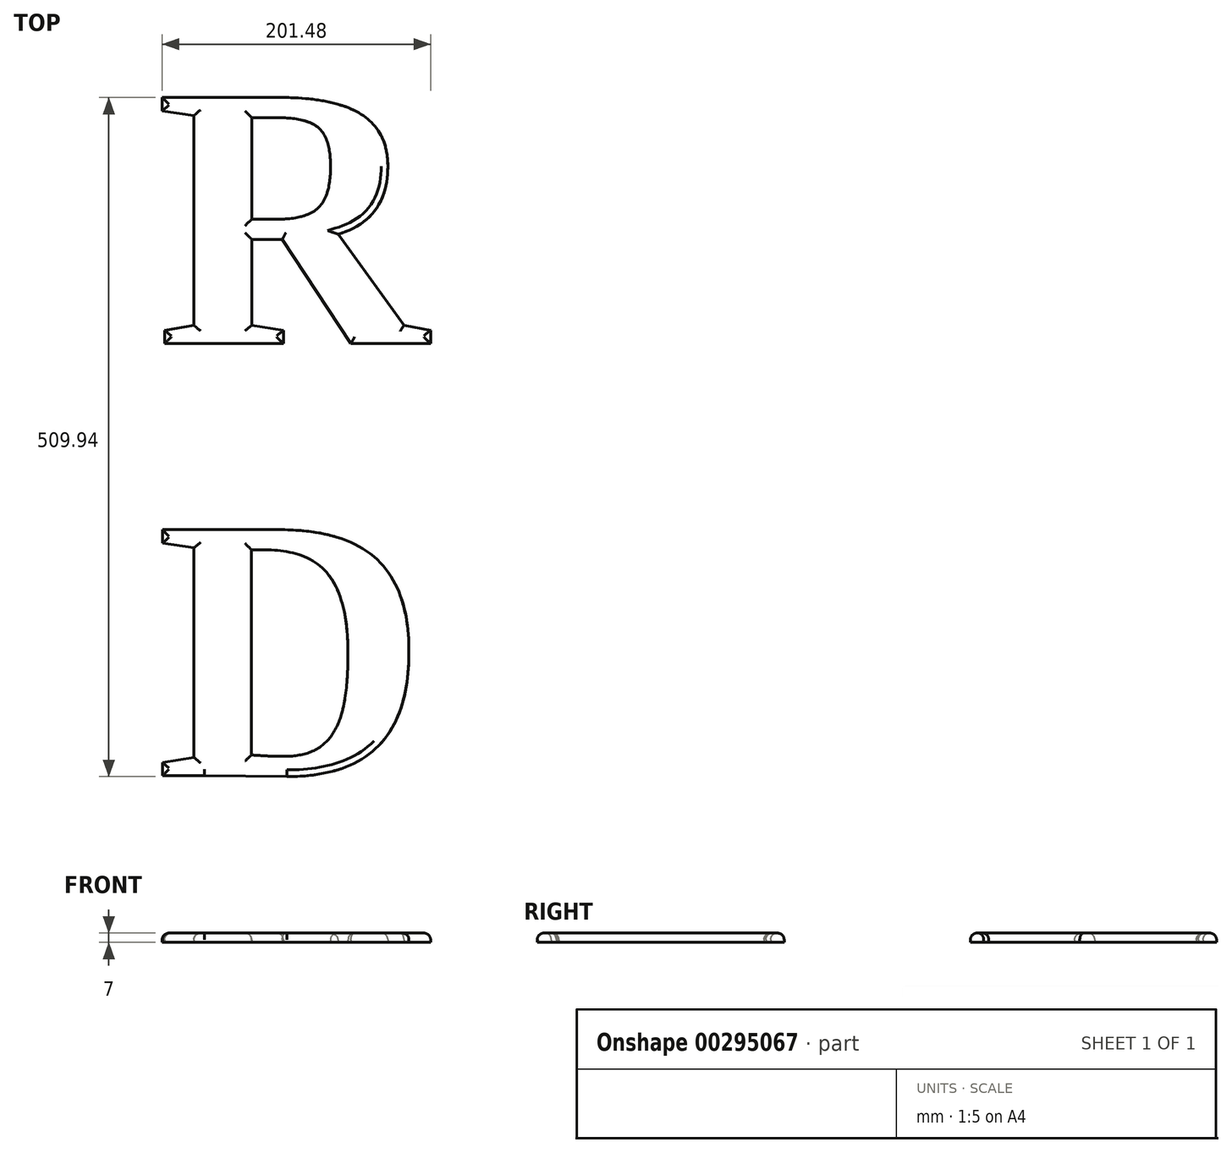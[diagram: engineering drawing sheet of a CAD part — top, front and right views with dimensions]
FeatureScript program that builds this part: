
annotation { "Feature Type Name" : "Feature", "Feature Type Description" : "" }
export const myFeature = defineFeature(function(context is Context, id is Id, definition is map)
    precondition{}
    {
        {
            var Q0;
            Q0=qCreatedBy(makeId("Top.planeOp"),FACE);
            var sketch = newSketch(context, id + "F0", { "sketchPlane" : qUnion([Q0])});
            skText(sketch, "E0", { "text": "R\nD", "fontName": "Tinos-Bold.ttf"});
            const initialGuessF0  = {"E0": [-0.22393, 0, 1, 0, 0.2032]};
            skSetInitialGuess(sketch, initialGuessF0);
            skSolve(sketch);
        }
        {
            var Q0;
            Q0=makeQuery(id+"F0.imprint","IMPRINT",FACE,{"disambiguationData":[TD([[makeQuery(id+"F0.imprint","IMPRINT",EDGE,{"derivedFrom":sQuery(id+"F0.wireOp",EDGE,"E0.sketch_text.stroke-0")}),-1.0]])]});
            var Q1;
            Q1=makeQuery(id+"F0.imprint","IMPRINT",FACE,{"disambiguationData":[TD([[makeQuery(id+"F0.imprint","IMPRINT",EDGE,{"derivedFrom":sQuery(id+"F0.wireOp",EDGE,"E0.sketch_text.stroke-26")}),-1.0]])]});
            extrude(context, id + "F1", {"entities" : qUnion([Q0, Q1]), "depth" : 7 * mm});
        }
        {
            var Q0;
            Q0=makeQuery(id+"F1.opExtrude","CAP_FACE",FACE,{"disambiguationData":[OSD([sQuery(id+"F0.wireOp",EDGE,"E0.sketch_text.stroke-0"),sQuery(id+"F0.wireOp",EDGE,"E0.sketch_text.stroke-1"),sQuery(id+"F0.wireOp",EDGE,"E0.sketch_text.stroke-2"),sQuery(id+"F0.wireOp",EDGE,"E0.sketch_text.stroke-3"),sQuery(id+"F0.wireOp",EDGE,"E0.sketch_text.stroke-4"),sQuery(id+"F0.wireOp",EDGE,"E0.sketch_text.stroke-5"),sQuery(id+"F0.wireOp",EDGE,"E0.sketch_text.stroke-6"),sQuery(id+"F0.wireOp",EDGE,"E0.sketch_text.stroke-7"),sQuery(id+"F0.wireOp",EDGE,"E0.sketch_text.stroke-8"),sQuery(id+"F0.wireOp",EDGE,"E0.sketch_text.stroke-9"),sQuery(id+"F0.wireOp",EDGE,"E0.sketch_text.stroke-10"),sQuery(id+"F0.wireOp",EDGE,"E0.sketch_text.stroke-11"),sQuery(id+"F0.wireOp",EDGE,"E0.sketch_text.stroke-12"),sQuery(id+"F0.wireOp",EDGE,"E0.sketch_text.stroke-13"),sQuery(id+"F0.wireOp",EDGE,"E0.sketch_text.stroke-14"),sQuery(id+"F0.wireOp",EDGE,"E0.sketch_text.stroke-15"),sQuery(id+"F0.wireOp",EDGE,"E0.sketch_text.stroke-16"),sQuery(id+"F0.wireOp",EDGE,"E0.sketch_text.stroke-17"),sQuery(id+"F0.wireOp",EDGE,"E0.sketch_text.stroke-18"),sQuery(id+"F0.wireOp",EDGE,"E0.sketch_text.stroke-19"),sQuery(id+"F0.wireOp",EDGE,"E0.sketch_text.stroke-20"),sQuery(id+"F0.wireOp",EDGE,"E0.sketch_text.stroke-21"),sQuery(id+"F0.wireOp",EDGE,"E0.sketch_text.stroke-22"),sQuery(id+"F0.wireOp",EDGE,"E0.sketch_text.stroke-23"),sQuery(id+"F0.wireOp",EDGE,"E0.sketch_text.stroke-24"),sQuery(id+"F0.wireOp",EDGE,"E0.sketch_text.stroke-25")])],"isStart":false});
            var Q1;
            Q1=makeQuery(id+"F1.opExtrude","CAP_FACE",FACE,{"disambiguationData":[OSD([sQuery(id+"F0.wireOp",EDGE,"E0.sketch_text.stroke-26"),sQuery(id+"F0.wireOp",EDGE,"E0.sketch_text.stroke-27"),sQuery(id+"F0.wireOp",EDGE,"E0.sketch_text.stroke-28"),sQuery(id+"F0.wireOp",EDGE,"E0.sketch_text.stroke-29"),sQuery(id+"F0.wireOp",EDGE,"E0.sketch_text.stroke-30"),sQuery(id+"F0.wireOp",EDGE,"E0.sketch_text.stroke-31"),sQuery(id+"F0.wireOp",EDGE,"E0.sketch_text.stroke-32"),sQuery(id+"F0.wireOp",EDGE,"E0.sketch_text.stroke-33"),sQuery(id+"F0.wireOp",EDGE,"E0.sketch_text.stroke-34"),sQuery(id+"F0.wireOp",EDGE,"E0.sketch_text.stroke-35"),sQuery(id+"F0.wireOp",EDGE,"E0.sketch_text.stroke-36"),sQuery(id+"F0.wireOp",EDGE,"E0.sketch_text.stroke-37"),sQuery(id+"F0.wireOp",EDGE,"E0.sketch_text.stroke-38"),sQuery(id+"F0.wireOp",EDGE,"E0.sketch_text.stroke-39"),sQuery(id+"F0.wireOp",EDGE,"E0.sketch_text.stroke-40"),sQuery(id+"F0.wireOp",EDGE,"E0.sketch_text.stroke-41"),sQuery(id+"F0.wireOp",EDGE,"E0.sketch_text.stroke-42"),sQuery(id+"F0.wireOp",EDGE,"E0.sketch_text.stroke-43"),sQuery(id+"F0.wireOp",EDGE,"E0.sketch_text.stroke-44"),sQuery(id+"F0.wireOp",EDGE,"E0.sketch_text.stroke-45")])],"isStart":false});
            fillet(context, id + "F2", {"entities" : qUnion([Q0, Q1]), "radius" : 5 * mm, "tangentPropagation" : true, "allowEdgeOverflow" : false});
        }
    });
